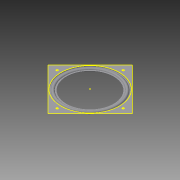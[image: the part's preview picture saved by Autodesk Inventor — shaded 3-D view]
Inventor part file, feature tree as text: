
AUTODESK INVENTOR PART (.ipt)
format: ipt  version: 2015 (Build 190159000, 159)  size: 152,576 bytes
history: native  units: in
note: dims shown in document units (in); Inventor stores cm internally (conversion verified against a paired STEP export)
features: other x1, sketch x1, imported_body x1
ambient origin geometry x8: Origin, YZ Plane, XZ Plane, XY Plane, X Axis, Y Axis, Z Axis, Center Point
bodies: Solid1 (feature_tree)
feature tree (3):
  other  "1544T100.sat1"
  sketch  "Sketch1"
  imported_body  "Base1"
